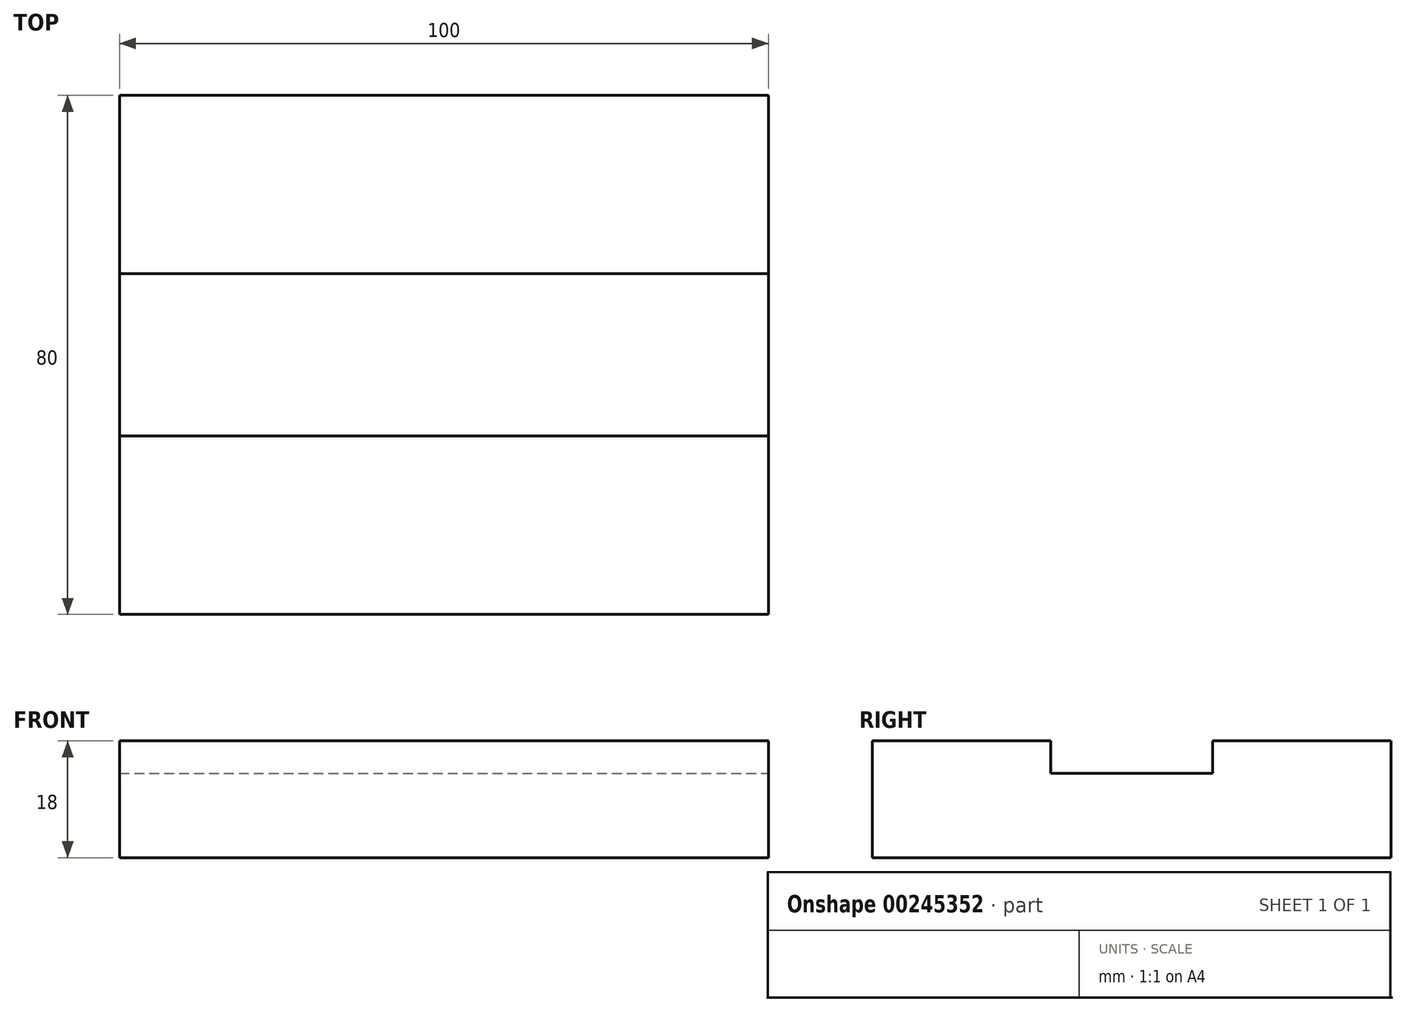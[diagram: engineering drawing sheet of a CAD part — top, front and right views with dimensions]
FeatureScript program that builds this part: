
annotation { "Feature Type Name" : "Feature", "Feature Type Description" : "" }
export const myFeature = defineFeature(function(context is Context, id is Id, definition is map)
    precondition{}
    {
        {
            var Q0;
            Q0=qCreatedBy(makeId("Top.planeOp"),FACE);
            var sketch = newSketch(context, id + "F0", { "sketchPlane" : qUnion([Q0])});
            skLineSegment(sketch, "E0.bottom", {"start": v(-50, -21.88) * mm, "end": v(50, -21.88) * mm});
            skLineSegment(sketch, "E0.top", {"start": v(-50, 58.12) * mm, "end": v(50, 58.12) * mm});
            skLineSegment(sketch, "E0.left", {"start": v(-50, -21.88) * mm, "end": v(-50, 58.12) * mm});
            skLineSegment(sketch, "E0.right", {"start": v(50, -21.88) * mm, "end": v(50, 58.12) * mm});
            skSolve(sketch);
        }
        {
            var Q0;
            Q0 = qSketchRegion(id + "F0", true);
            extrude(context, id + "F1", {"entities" : qUnion([Q0]), "depth" : 18 * mm});
        }
        {
            var Q0;
            Q0=makeQuery(id+"F1.opExtrude","SWEPT_FACE",FACE,{"disambiguationData":[OSD([sQuery(id+"F0.wireOp",EDGE,"E0.right")])]});
            var sketch = newSketch(context, id + "F2", { "sketchPlane" : qUnion([Q0])});
            skLineSegment(sketch, "E1.right", {"start": v(30.62, 23) * mm, "end": v(30.62, 13) * mm});
            skLineSegment(sketch, "E2", {"start": v(30.62, 23) * mm, "end": v(5.62, 23) * mm});
            skLineSegment(sketch, "E3", {"start": v(5.62, 23) * mm, "end": v(5.62, 13) * mm});
            skLineSegment(sketch, "E4", {"start": v(5.62, 13) * mm, "end": v(30.62, 13) * mm});
            skSolve(sketch);
        }
        {
            var Q0;
            Q0 = qSketchRegion(id + "F2", true);
            extrude(context, id + "F3", {"entities" : qUnion([Q0]), "operationType" : NewBodyOperationType.REMOVE, "endBound" : BoundingType.THROUGH_ALL, "oppositeDirection" : true, "depth" : 25 * mm});
        }
    });
